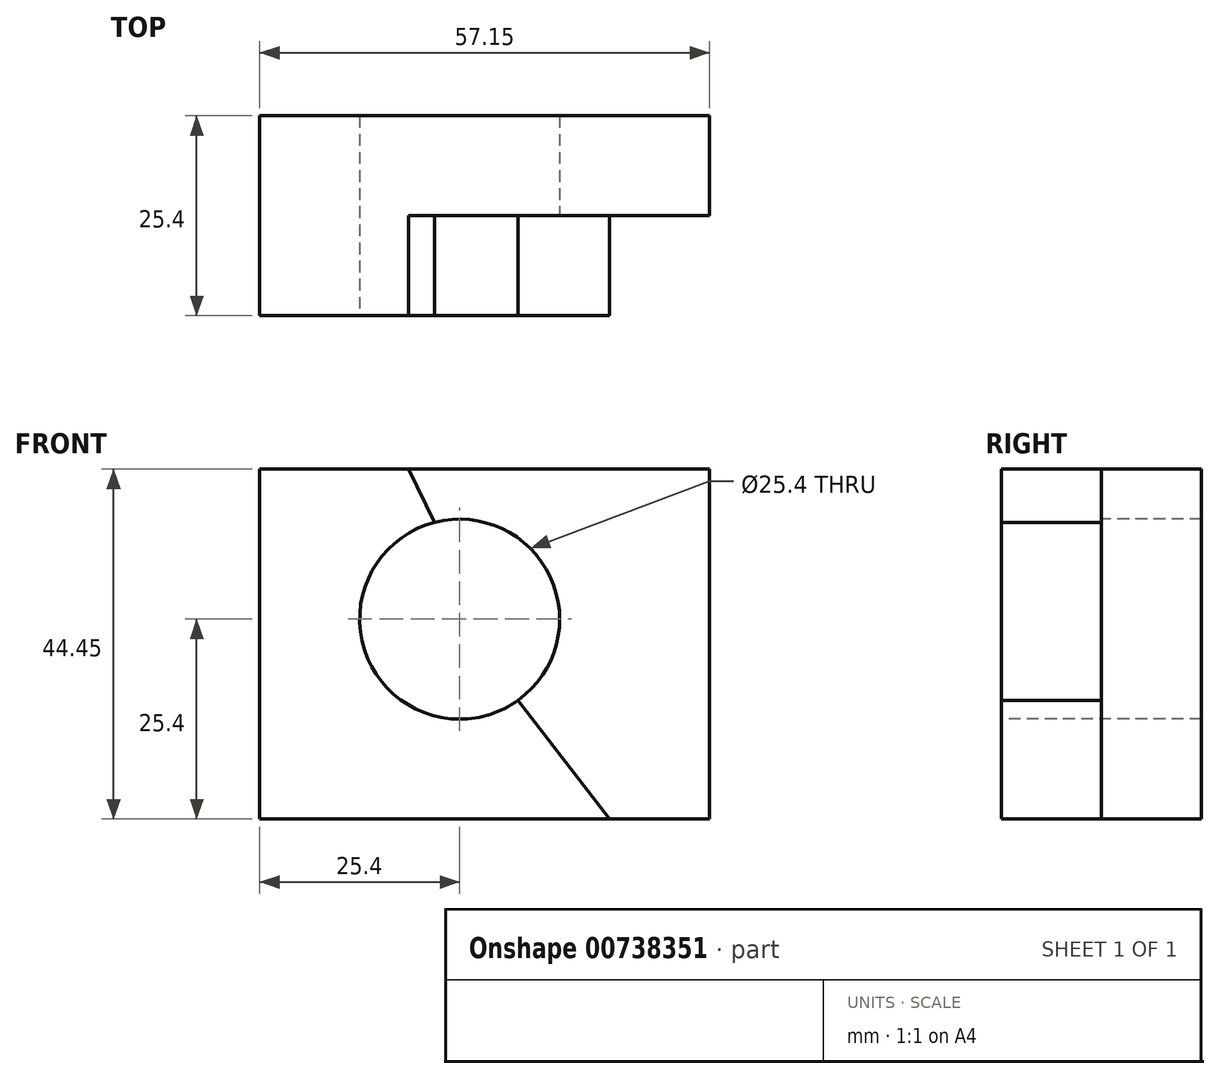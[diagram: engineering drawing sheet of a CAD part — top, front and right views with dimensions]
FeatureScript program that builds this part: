
annotation { "Feature Type Name" : "Feature", "Feature Type Description" : "" }
export const myFeature = defineFeature(function(context is Context, id is Id, definition is map)
    precondition{}
    {
        {
            var Q0;
            Q0=qCreatedBy(makeId("Front.planeOp"),FACE);
            var sketch = newSketch(context, id + "F0", { "sketchPlane" : qUnion([Q0])});
            skLineSegment(sketch, "E0", {"start": v(0, 0) * mm, "end": v(0, 44.45) * mm});
            skLineSegment(sketch, "E1", {"start": v(0, 44.45) * mm, "end": v(57.15, 44.45) * mm});
            skLineSegment(sketch, "E2", {"start": v(57.15, 44.45) * mm, "end": v(57.15, 0) * mm});
            skLineSegment(sketch, "E3", {"start": v(57.15, 0) * mm, "end": v(0, 0) * mm});
            skSolve(sketch);
        }
        {
            var Q0;
            Q0 = qSketchRegion(id + "F0", true);
            extrude(context, id + "F1", {"entities" : qUnion([Q0]), "depth" : 25.4 * mm, "offsetDistance" : 25.4 * mm});
        }
        {
            var Q0;
            Q0=makeQuery(id+"F1.opExtrude","CAP_FACE",FACE,{"disambiguationData":[OSD([sQuery(id+"F0.wireOp",EDGE,"E0"),sQuery(id+"F0.wireOp",EDGE,"E1"),sQuery(id+"F0.wireOp",EDGE,"E2"),sQuery(id+"F0.wireOp",EDGE,"E3")])],"isStart":false});
            var sketch = newSketch(context, id + "F2", { "sketchPlane" : qUnion([Q0])});
            skLineSegment(sketch, "E4", {"start": v(0, 44.45) * mm, "end": v(25.4, 44.45) * mm});
            skLineSegment(sketch, "E5", {"start": v(25.4, 44.45) * mm, "end": v(25.4, 25.4) * mm});
            skCircle(sketch, "E6", {"center": v(25.4, 25.4) * mm, "radius": 12.7 * mm});
            skSolve(sketch);
        }
        {
            var Q0;
            Q0 = qSketchRegion(id + "F2", true);
            extrude(context, id + "F3", {"entities" : qUnion([Q0]), "operationType" : NewBodyOperationType.REMOVE, "endBound" : BoundingType.THROUGH_ALL, "oppositeDirection" : true, "depth" : 25.4 * mm, "offsetDistance" : 25.4 * mm});
        }
        {
            var Q0;
            Q0=makeQuery(id+"F1.opExtrude","CAP_FACE",FACE,{"disambiguationData":[OSD([sQuery(id+"F0.wireOp",EDGE,"E0"),sQuery(id+"F0.wireOp",EDGE,"E1"),sQuery(id+"F0.wireOp",EDGE,"E2"),sQuery(id+"F0.wireOp",EDGE,"E3")])],"isStart":false});
            var sketch = newSketch(context, id + "F4", { "sketchPlane" : qUnion([Q0])});
            skLineSegment(sketch, "E7", {"start": v(0, 44.45) * mm, "end": v(18.94, 44.45) * mm});
            skLineSegment(sketch, "E8", {"start": v(18.94, 44.45) * mm, "end": v(22.23, 37.7) * mm});
            skLineSegment(sketch, "E9", {"start": v(22.23, 37.7) * mm, "end": v(0, 37.7) * mm});
            skLineSegment(sketch, "E10", {"start": v(32.84, 15.1) * mm, "end": v(44.45, 0) * mm});
            skLineSegment(sketch, "E11", {"start": v(44.45, 0) * mm, "end": v(57.15, 0) * mm});
            skSolve(sketch);
        }
        {
            var Q0;
            Q0 = qSketchRegion(id + "F4", true);
            var Q1;
            {var subQ2=sQuery(id+"F4.wireOp",EDGE,"E8");Q1=makeQuery(id+"F4.imprint","IMPRINT",FACE,{"disambiguationData":[TD([[makeQuery(id+"F4.imprint","IMPRINT",EDGE,{"derivedFrom":subQ2}),1.0]])]});}
            extrude(context, id + "F5", {"entities" : qUnion([Q0, Q1]), "operationType" : NewBodyOperationType.REMOVE, "oppositeDirection" : true, "depth" : 12.7 * mm, "offsetDistance" : 25.4 * mm});
        }
    });
